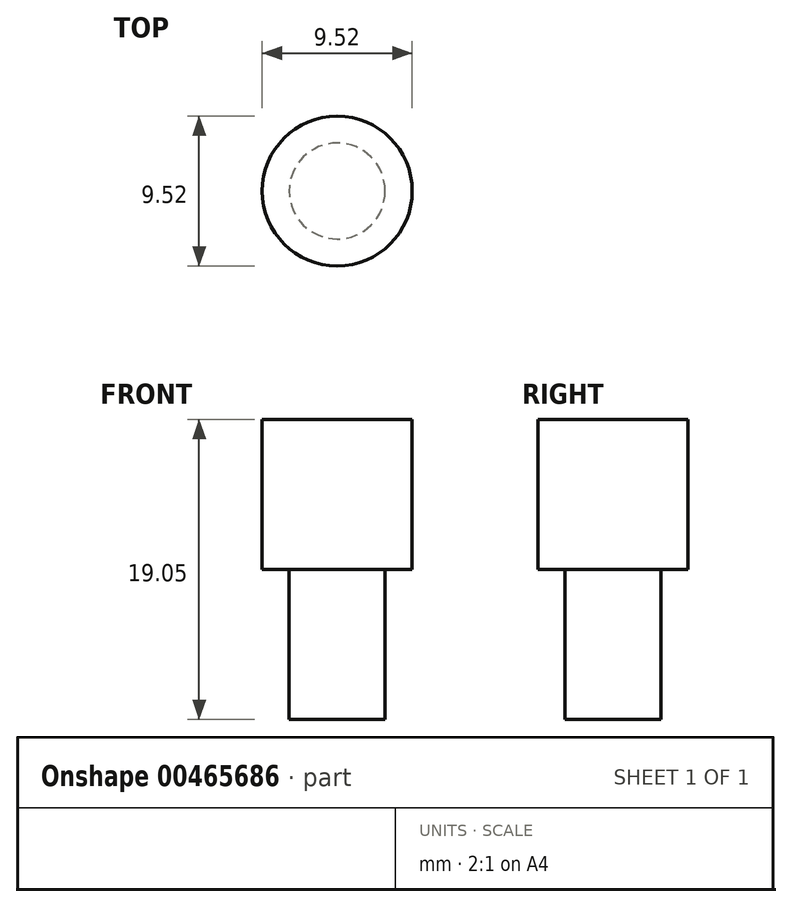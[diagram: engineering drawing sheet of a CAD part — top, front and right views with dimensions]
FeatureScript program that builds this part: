
annotation { "Feature Type Name" : "Feature", "Feature Type Description" : "" }
export const myFeature = defineFeature(function(context is Context, id is Id, definition is map)
    precondition{}
    {
        {
            var Q0;
            Q0=qCreatedBy(makeId("Top.planeOp"),FACE);
            var sketch = newSketch(context, id + "F0", { "sketchPlane" : qUnion([Q0])});
            skCircle(sketch, "E0", {"center": v(0, 0) * mm, "radius": 3.05 * mm});
            skSolve(sketch);
        }
        {
            var Q0;
            Q0 = qSketchRegion(id + "F0", true);
            extrude(context, id + "F1", {"entities" : qUnion([Q0]), "endBound" : BoundingType.SYMMETRIC, "oppositeDirection" : true, "depth" : 9.52 * mm});
        }
        {
            var Q0;
            Q0=makeQuery(id+"F1.opExtrude","CAP_FACE",FACE,{"disambiguationData":[OSD([sQuery(id+"F0.wireOp",EDGE,"E0")])],"isStart":true});
            var sketch = newSketch(context, id + "F2", { "sketchPlane" : qUnion([Q0])});
            skCircle(sketch, "E1", {"center": v(0, 0) * mm, "radius": 4.76 * mm});
            skSolve(sketch);
        }
        {
            var Q0;
            Q0 = qSketchRegion(id + "F2", true);
            extrude(context, id + "F3", {"entities" : qUnion([Q0]), "operationType" : NewBodyOperationType.ADD, "depth" : 9.52 * mm});
        }
        {
            var Q0;
            Q0=makeQuery(id+"F3.opExtrude","CAP_FACE",FACE,{"disambiguationData":[OSD([sQuery(id+"F2.wireOp",EDGE,"E1")])],"isStart":false});
            var sketch = newSketch(context, id + "F4", { "sketchPlane" : qUnion([Q0])});
            skCircle(sketch, "E2", {"center": v(0, 0) * mm, "radius": 2.54 * mm});
            skCircle(sketch, "E3.0", {"center": v(0, 0) * mm, "radius": 1.46 * mm});
            skSolve(sketch);
        }
        {
            var Q0;
            Q0 = qSketchRegion(id + "F4", true);
            extrude(context, id + "F5", {"entities" : qUnion([Q0]), "operationType" : NewBodyOperationType.REMOVE, "oppositeDirection" : true, "depth" : 1 / 812.8 * mm});
        }
    });
